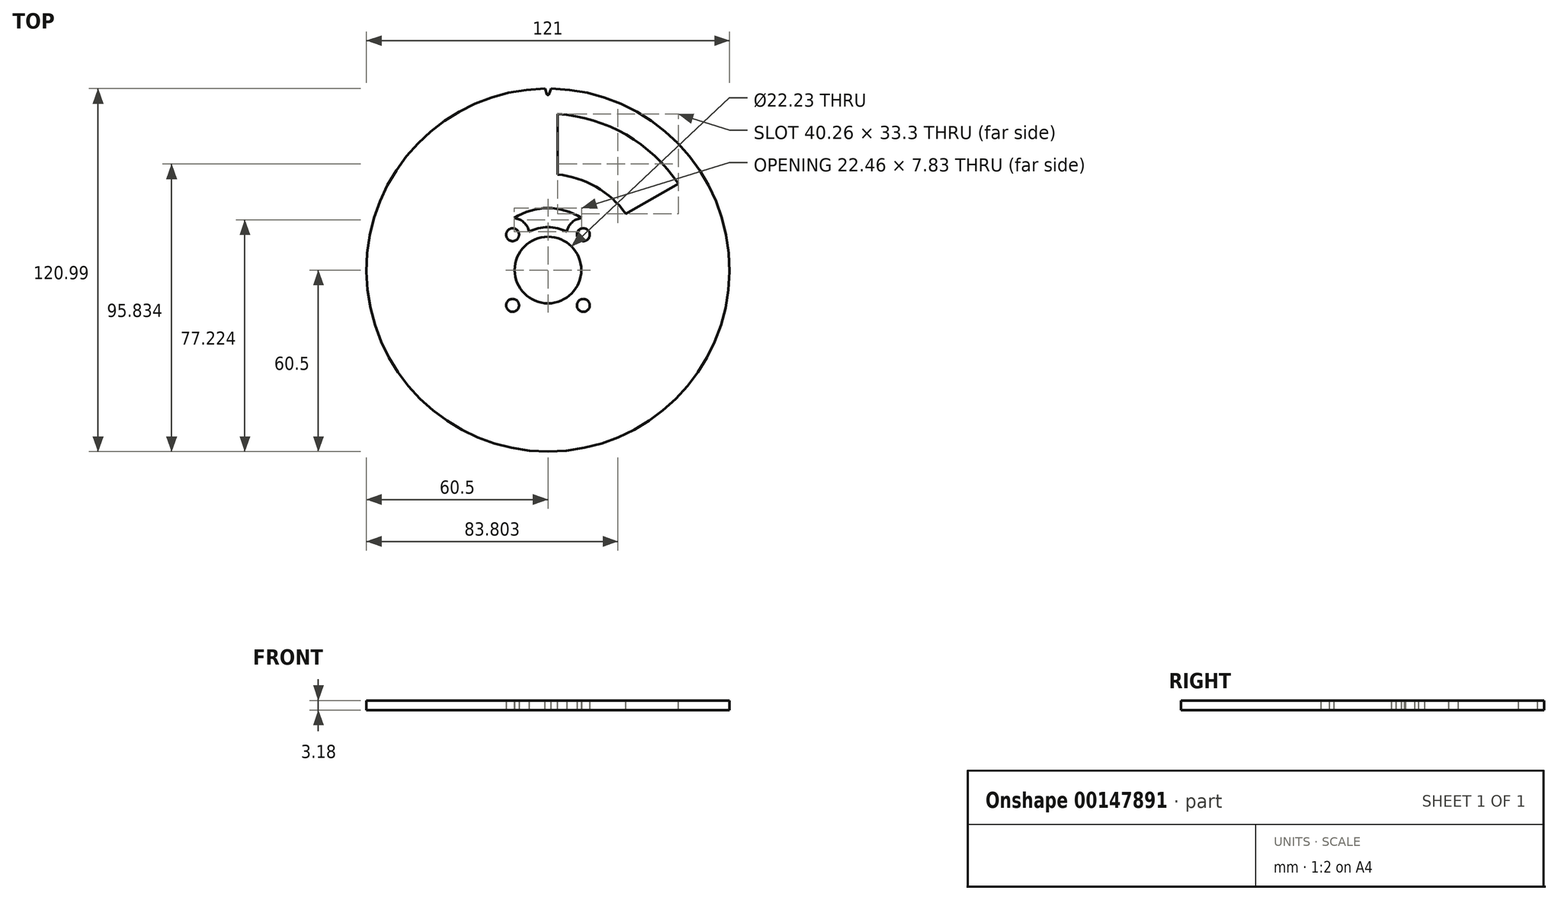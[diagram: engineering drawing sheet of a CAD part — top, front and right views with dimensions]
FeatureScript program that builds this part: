
annotation { "Feature Type Name" : "Feature", "Feature Type Description" : "" }
export const myFeature = defineFeature(function(context is Context, id is Id, definition is map)
    precondition{}
    {
        {
            var Q0;
            Q0=qCreatedBy(makeId("Top.planeOp"),FACE);
            var sketch = newSketch(context, id + "F0", { "sketchPlane" : qUnion([Q0])});
            skCircle(sketch, "E0", {"center": v(0, 0) * mm, "radius": 60.5 * mm});
            skCircle(sketch, "E1", {"center": v(0, 0) * mm, "radius": 11.11 * mm});
            skLineSegment(sketch, "E2.bottom", {"start": v(-11.79, -11.79) * mm, "end": v(11.79, -11.79) * mm, "construction": true});
            skLineSegment(sketch, "E2.top", {"start": v(-11.79, 11.79) * mm, "end": v(11.79, 11.79) * mm, "construction": true});
            skLineSegment(sketch, "E2.left", {"start": v(-11.79, -11.79) * mm, "end": v(-11.79, 11.79) * mm, "construction": true});
            skLineSegment(sketch, "E2.right", {"start": v(11.79, -11.79) * mm, "end": v(11.79, 11.79) * mm, "construction": true});
            skCircle(sketch, "E3", {"center": v(-11.79, -11.79) * mm, "radius": 5.56 * mm, "construction": true});
            skCircle(sketch, "E4", {"center": v(-11.79, -11.79) * mm, "radius": 2.15 * mm});
            skCircle(sketch, "E5", {"center": v(11.79, 11.79) * mm, "radius": 2.15 * mm});
            skCircle(sketch, "E6", {"center": v(11.79, -11.79) * mm, "radius": 2.15 * mm});
            skCircle(sketch, "E7", {"center": v(-11.79, 11.79) * mm, "radius": 2.15 * mm});
            skSolve(sketch);
        }
        {
            var Q0;
            Q0=makeQuery(id+"F0.imprint","IMPRINT",FACE,{"disambiguationData":[TD([[makeQuery(id+"F0.imprint","IMPRINT",EDGE,{"derivedFrom":sQuery(id+"F0.wireOp",EDGE,"d7zeTPih-CRss-xDOh-gPdP-rmPCdwzH7cdN.left")}),1.0]])]});
            var Q1;
            Q1=makeQuery(id+"F0.imprint","IMPRINT",FACE,{"disambiguationData":[TD([[makeQuery(id+"F0.imprint","IMPRINT",EDGE,{"derivedFrom":sQuery(id+"F0.wireOp",EDGE,"E0")}),1.0]])]});
            extrude(context, id + "F1", {"entities" : qUnion([Q0, Q1]), "depth" : 3.17 * mm});
        }
        {
            var Q0;
            Q0=makeQuery(id+"F1.opExtrude","CAP_FACE",FACE,{"disambiguationData":[OSD([sQuery(id+"F0.wireOp",EDGE,"d7zeTPih-CRss-xDOh-gPdP-rmPCdwzH7cdN.left"),sQuery(id+"F0.wireOp",EDGE,"d7zeTPih-CRss-xDOh-gPdP-rmPCdwzH7cdN.right"),sQuery(id+"F0.wireOp",EDGE,"ScfBMfkV-s1yN-Ls9R-SGr5-fEyGpD6zak8e"),sQuery(id+"F0.wireOp",EDGE,"xnxmVwjl-FvSF-m7sj-be2U-u85gZZGoORGZ"),sQuery(id+"F0.wireOp",EDGE,"E0")])],"isStart":false});
            var sketch = newSketch(context, id + "F2", { "sketchPlane" : qUnion([Q0])});
            skLineSegment(sketch, "E8", {"start": v(0, 0) * mm, "end": v(0, 60.5) * mm, "construction": true});
            skLineSegment(sketch, "E9", {"start": v(0, 0) * mm, "end": v(0.66, 60.5) * mm, "construction": true});
            skArc(sketch, "E10", {"start": v(1.02, 60.5) * mm, "mid": v(0, 60.5) * mm, "end": v(-1.02, 60.5) * mm});
            skLineSegment(sketch, "E11", {"start": v(-1.02, 60.5) * mm, "end": v(-0.28, 58.52) * mm});
            skLineSegment(sketch, "E12", {"start": v(1.02, 60.5) * mm, "end": v(0.28, 58.52) * mm});
            skPoint(sketch, "E13", {"position": v(0.65, 59.5) * mm});
            skArc(sketch, "E14", {"start": v(-0.28, 58.52) * mm, "mid": v(0, 58.33) * mm, "end": v(0.28, 58.52) * mm});
            skSolve(sketch);
        }
        {
            var Q0;
            Q0=qSketchRegion(id+"F2",true);
            var Q1;
            Q1=makeQuery(id+"F1.opExtrude","CAP_FACE",FACE,{"disambiguationData":[OSD([sQuery(id+"F0.wireOp",EDGE,"d7zeTPih-CRss-xDOh-gPdP-rmPCdwzH7cdN.left"),sQuery(id+"F0.wireOp",EDGE,"d7zeTPih-CRss-xDOh-gPdP-rmPCdwzH7cdN.right"),sQuery(id+"F0.wireOp",EDGE,"ScfBMfkV-s1yN-Ls9R-SGr5-fEyGpD6zak8e"),sQuery(id+"F0.wireOp",EDGE,"xnxmVwjl-FvSF-m7sj-be2U-u85gZZGoORGZ"),sQuery(id+"F0.wireOp",EDGE,"E0")])],"isStart":true});
            extrude(context, id + "F3", {"entities" : qUnion([Q0]), "operationType" : NewBodyOperationType.REMOVE, "endBound" : BoundingType.UP_TO_SURFACE, "oppositeDirection" : true, "endBoundEntityFace" : qUnion([Q1]), "depth" : 25.4 * mm});
        }
        {
            var Q0;
            Q0=makeQuery(id+"F1.opExtrude","CAP_FACE",FACE,{"disambiguationData":[OSD([sQuery(id+"F0.wireOp",EDGE,"E0"),sQuery(id+"F0.wireOp",EDGE,"E1"),sQuery(id+"F0.wireOp",EDGE,"E4"),sQuery(id+"F0.wireOp",EDGE,"E5"),sQuery(id+"F0.wireOp",EDGE,"E6"),sQuery(id+"F0.wireOp",EDGE,"E7")])],"isStart":false});
            var sketch = newSketch(context, id + "F4", { "sketchPlane" : qUnion([Q0])});
            skLineSegment(sketch, "E15", {"start": v(0, 0) * mm, "end": v(0, 31.87) * mm, "construction": true});
            skLineSegment(sketch, "E16", {"start": v(0, 31.87) * mm, "end": v(3.18, 31.87) * mm, "construction": true});
            skLineSegment(sketch, "E17", {"start": v(3.17, 51.98) * mm, "end": v(0, 51.98) * mm, "construction": true});
            skLineSegment(sketch, "E18", {"start": v(0, 51.98) * mm, "end": v(0, 58.33) * mm, "construction": true});
            skLineSegment(sketch, "E19", {"start": v(0, 0) * mm, "end": v(27.6, 15.94) * mm, "construction": true});
            skCircle(sketch, "E20", {"center": v(0, 0) * mm, "radius": 58.33 * mm, "construction": true});
            skLineSegment(sketch, "E21", {"start": v(27.6, 15.94) * mm, "end": v(26.01, 18.69) * mm, "construction": true});
            skArc(sketch, "E22", {"start": v(26.01, 18.69) * mm, "mid": v(16.01, 27.74) * mm, "end": v(3.18, 31.87) * mm});
            skLineSegment(sketch, "E23", {"start": v(3.18, 31.87) * mm, "end": v(3.18, 51.98) * mm});
            skLineSegment(sketch, "E24", {"start": v(26.01, 18.69) * mm, "end": v(43.43, 28.74) * mm});
            skArc(sketch, "E25", {"start": v(43.43, 28.74) * mm, "mid": v(26.04, 45.1) * mm, "end": v(3.18, 51.98) * mm});
            skSolve(sketch);
        }
        {
            var Q0;
            Q0=qSketchRegion(id+"F4",true);
            var Q1;
            Q1=makeQuery(id+"F1.opExtrude","CAP_FACE",FACE,{"disambiguationData":[OSD([sQuery(id+"F0.wireOp",EDGE,"E0"),sQuery(id+"F0.wireOp",EDGE,"E1"),sQuery(id+"F0.wireOp",EDGE,"E4"),sQuery(id+"F0.wireOp",EDGE,"E5"),sQuery(id+"F0.wireOp",EDGE,"E6"),sQuery(id+"F0.wireOp",EDGE,"E7")])],"isStart":true});
            extrude(context, id + "F5", {"entities" : qUnion([Q0]), "operationType" : NewBodyOperationType.REMOVE, "endBound" : BoundingType.UP_TO_SURFACE, "oppositeDirection" : true, "endBoundEntityFace" : qUnion([Q1]), "depth" : 25.4 * mm});
        }
        {
            var Q0;
            Q0=makeQuery(id+"F1.opExtrude","CAP_FACE",FACE,{"disambiguationData":[OSD([sQuery(id+"F0.wireOp",EDGE,"E0"),sQuery(id+"F0.wireOp",EDGE,"E1"),sQuery(id+"F0.wireOp",EDGE,"E4"),sQuery(id+"F0.wireOp",EDGE,"E5"),sQuery(id+"F0.wireOp",EDGE,"E6"),sQuery(id+"F0.wireOp",EDGE,"E7")])],"isStart":true});
            var sketch = newSketch(context, id + "F6", { "sketchPlane" : qUnion([Q0])});
            skArc(sketch, "E26", {"start": v(6.33, -12.81) * mm, "mid": v(8.03, -15.88) * mm, "end": v(11.23, -17.31) * mm});
            skArc(sketch, "E27", {"start": v(-11.23, -17.31) * mm, "mid": v(-8.03, -15.88) * mm, "end": v(-6.33, -12.81) * mm});
            skArc(sketch, "E28", {"start": v(-6.33, -12.81) * mm, "mid": v(0, -14.29) * mm, "end": v(6.33, -12.81) * mm});
            skArc(sketch, "E29", {"start": v(-11.23, -17.31) * mm, "mid": v(0, -20.64) * mm, "end": v(11.23, -17.31) * mm});
            skSolve(sketch);
        }
        {
            var Q0;
            Q0=qSketchRegion(id+"F6",true);
            var Q1;
            Q1=makeQuery(id+"F1.opExtrude","CAP_FACE",FACE,{"disambiguationData":[OSD([sQuery(id+"F0.wireOp",EDGE,"E0"),sQuery(id+"F0.wireOp",EDGE,"E1"),sQuery(id+"F0.wireOp",EDGE,"E4"),sQuery(id+"F0.wireOp",EDGE,"E5"),sQuery(id+"F0.wireOp",EDGE,"E6"),sQuery(id+"F0.wireOp",EDGE,"E7")])],"isStart":false});
            extrude(context, id + "F7", {"entities" : qUnion([Q0]), "operationType" : NewBodyOperationType.REMOVE, "endBound" : BoundingType.UP_TO_SURFACE, "oppositeDirection" : true, "endBoundEntityFace" : qUnion([Q1]), "depth" : 25.4 * mm});
        }
    });
